# Revit family: Ribbeelement - P-dæk
name_source: partatom
category: Structural Framing
units: mm (PartAtom-declared; Revit-internal decimal feet)

## family parameters
Always export as geometry = No
Always vertical = Yes
Cut with Voids When Loaded = No
Material for Model Behavior = Other
OmniClass Number = 23.25.30.11.14.14
OmniClass Title = Beams
Section Shape = Not Defined
Shared = No
Show family pre-cut in plan views = Yes

## types (1)
- Ribbeelement - P-dæk
    Height = 600 mm
    Length Max = 17200 mm  [stored 56.4304 ft]
    Length Max Center = 2990 mm  [stored 9.80971 ft]
    Length Max Sloped = 5300 mm  [stored 17.3885 ft]
    Manufacturer = CRH Concrete
    Model = P
    Pladetykkelse = 110 mm  [stored 0.360892 ft]
    Width = 2480 mm  [stored 8.13648 ft]
    _OffsetWebCenter = 90 mm  [stored 0.295276 ft]
    _PlateThicknessStandard = 110 mm  [stored 0.360892 ft]
    _SlopeBottom = 0.030303
    _SlopeTop = 0.008333
    _TypeSidewalkNon = Fortov : Intet

note: [stored X ft] marks values corroborated as IEEE doubles in the binary element streams (Revit-internal decimal feet)

## geometry (parser evidence)
native form markers: Sweep x44
no freeform markers — native parametric forms only
